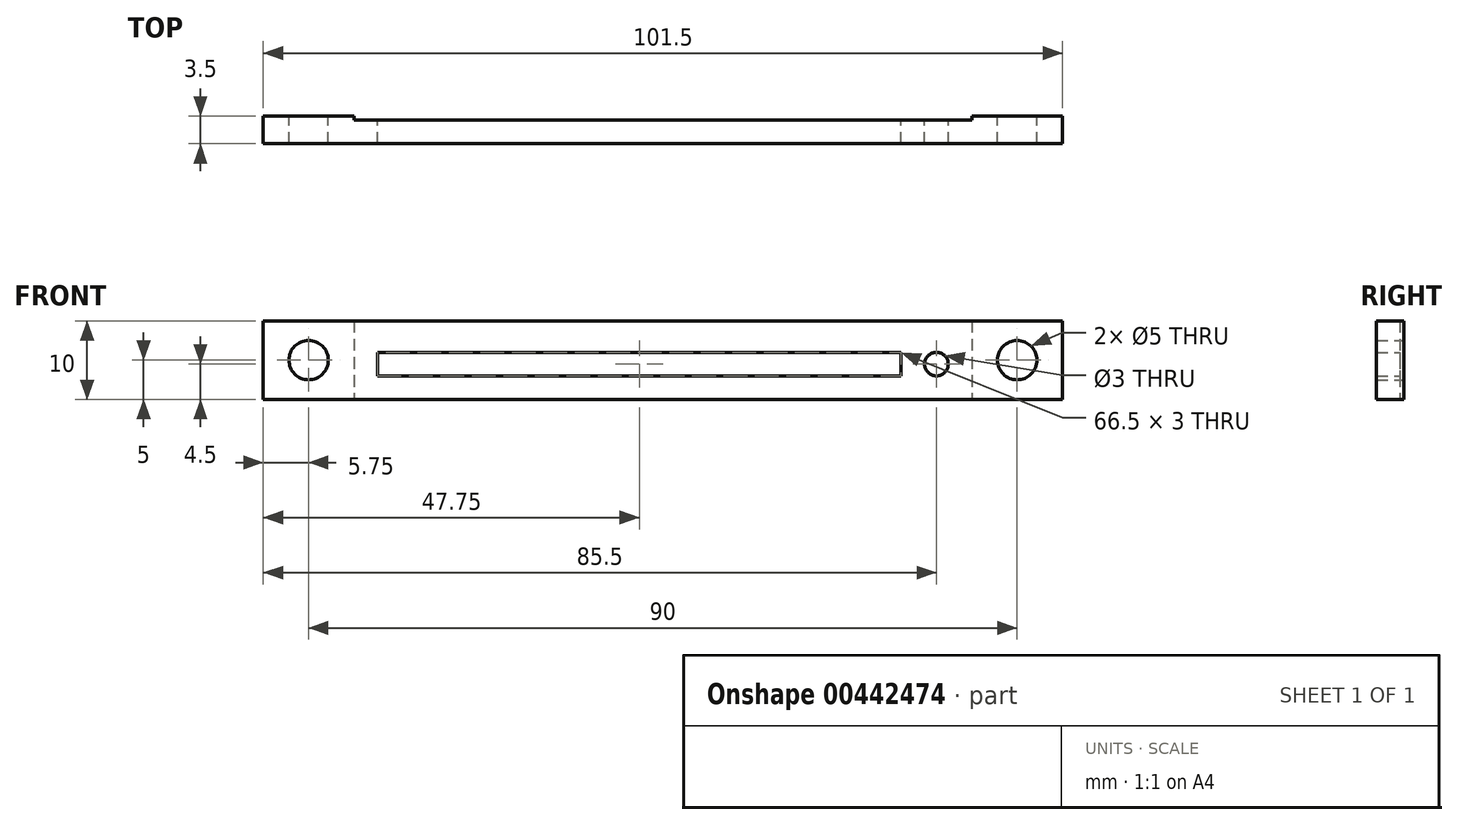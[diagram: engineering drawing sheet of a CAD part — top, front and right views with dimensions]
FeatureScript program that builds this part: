
annotation { "Feature Type Name" : "Feature", "Feature Type Description" : "" }
export const myFeature = defineFeature(function(context is Context, id is Id, definition is map)
    precondition{}
    {
        {
            var Q0;
            Q0=qCreatedBy(makeId("Front.planeOp"),FACE);
            var sketch = newSketch(context, id + "F0", { "sketchPlane" : qUnion([Q0])});
            skLineSegment(sketch, "E0.bottom", {"start": v(50.75, 5) * mm, "end": v(-50.75, 5) * mm});
            skLineSegment(sketch, "E0.top", {"start": v(50.75, -5) * mm, "end": v(-50.75, -5) * mm});
            skLineSegment(sketch, "E0.left", {"start": v(50.75, 5) * mm, "end": v(50.75, -5) * mm});
            skLineSegment(sketch, "E0.right", {"start": v(-50.75, 5) * mm, "end": v(-50.75, -5) * mm});
            skPoint(sketch, "E0.middle", {"position": v(0, 0) * mm});
            skLineSegment(sketch, "E1.bottom", {"start": v(39.25, 5) * mm, "end": v(-39.25, 5) * mm, "construction": true});
            skLineSegment(sketch, "E1.top", {"start": v(39.25, -5) * mm, "end": v(-39.25, -5) * mm, "construction": true});
            skLineSegment(sketch, "E1.left", {"start": v(39.25, 5) * mm, "end": v(39.25, -5) * mm, "construction": true});
            skLineSegment(sketch, "E1.right", {"start": v(-39.25, 5) * mm, "end": v(-39.25, -5) * mm, "construction": true});
            skLineSegment(sketch, "E2", {"start": v(50.75, 5) * mm, "end": v(39.25, -5) * mm, "construction": true});
            skLineSegment(sketch, "E3", {"start": v(39.25, 5) * mm, "end": v(50.75, -5) * mm, "construction": true});
            skLineSegment(sketch, "E4", {"start": v(-39.25, -5) * mm, "end": v(-50.75, 5) * mm, "construction": true});
            skLineSegment(sketch, "E5", {"start": v(-39.25, 5) * mm, "end": v(-50.75, -5) * mm, "construction": true});
            skCircle(sketch, "E6", {"center": v(-45, 0) * mm, "radius": 2.5 * mm});
            skCircle(sketch, "E7", {"center": v(45, 0) * mm, "radius": 2.5 * mm});
            skCircle(sketch, "E8", {"center": v(34.75, -0.5) * mm, "radius": 1.5 * mm});
            skLineSegment(sketch, "E9.bottom", {"start": v(30.25, -2) * mm, "end": v(-36.25, -2) * mm});
            skLineSegment(sketch, "E9.top", {"start": v(30.25, 1) * mm, "end": v(-36.25, 1) * mm});
            skLineSegment(sketch, "E9.left", {"start": v(30.25, -2) * mm, "end": v(30.25, 1) * mm});
            skLineSegment(sketch, "E9.right", {"start": v(-36.25, -2) * mm, "end": v(-36.25, 1) * mm});
            skSolve(sketch);
        }
        {
            var Q0;
            Q0 = qSketchRegion(id + "F0", true);
            extrude(context, id + "F1", {"entities" : qUnion([Q0]), "depth" : 3.5 * mm});
        }
        {
            var Q0;
            Q0=makeQuery(id+"F1.opExtrude","CAP_FACE",FACE,{"disambiguationData":[OSD([sQuery(id+"F0.wireOp",EDGE,"E0.bottom"),sQuery(id+"F0.wireOp",EDGE,"E0.top"),sQuery(id+"F0.wireOp",EDGE,"E0.left"),sQuery(id+"F0.wireOp",EDGE,"E0.right"),sQuery(id+"F0.wireOp",EDGE,"E6"),sQuery(id+"F0.wireOp",EDGE,"E7"),sQuery(id+"F0.wireOp",EDGE,"E8"),sQuery(id+"F0.wireOp",EDGE,"E9.bottom"),sQuery(id+"F0.wireOp",EDGE,"E9.top"),sQuery(id+"F0.wireOp",EDGE,"E9.left"),sQuery(id+"F0.wireOp",EDGE,"E9.right")])],"isStart":true});
            var sketch = newSketch(context, id + "F2", { "sketchPlane" : qUnion([Q0])});
            skLineSegment(sketch, "E10.bottom", {"start": v(39.25, 5) * mm, "end": v(-39.25, 5) * mm});
            skLineSegment(sketch, "E10.top", {"start": v(39.25, -5) * mm, "end": v(-39.25, -5) * mm});
            skLineSegment(sketch, "E10.left", {"start": v(39.25, 5) * mm, "end": v(39.25, -5) * mm});
            skLineSegment(sketch, "E10.right", {"start": v(-39.25, 5) * mm, "end": v(-39.25, -5) * mm});
            skPoint(sketch, "E10.middle", {"position": v(0, 0) * mm});
            skSolve(sketch);
        }
        {
            var Q0;
            Q0 = qSketchRegion(id + "F2", true);
            extrude(context, id + "F3", {"entities" : qUnion([Q0]), "operationType" : NewBodyOperationType.REMOVE, "oppositeDirection" : true, "depth" : .5 * mm});
        }
    });
